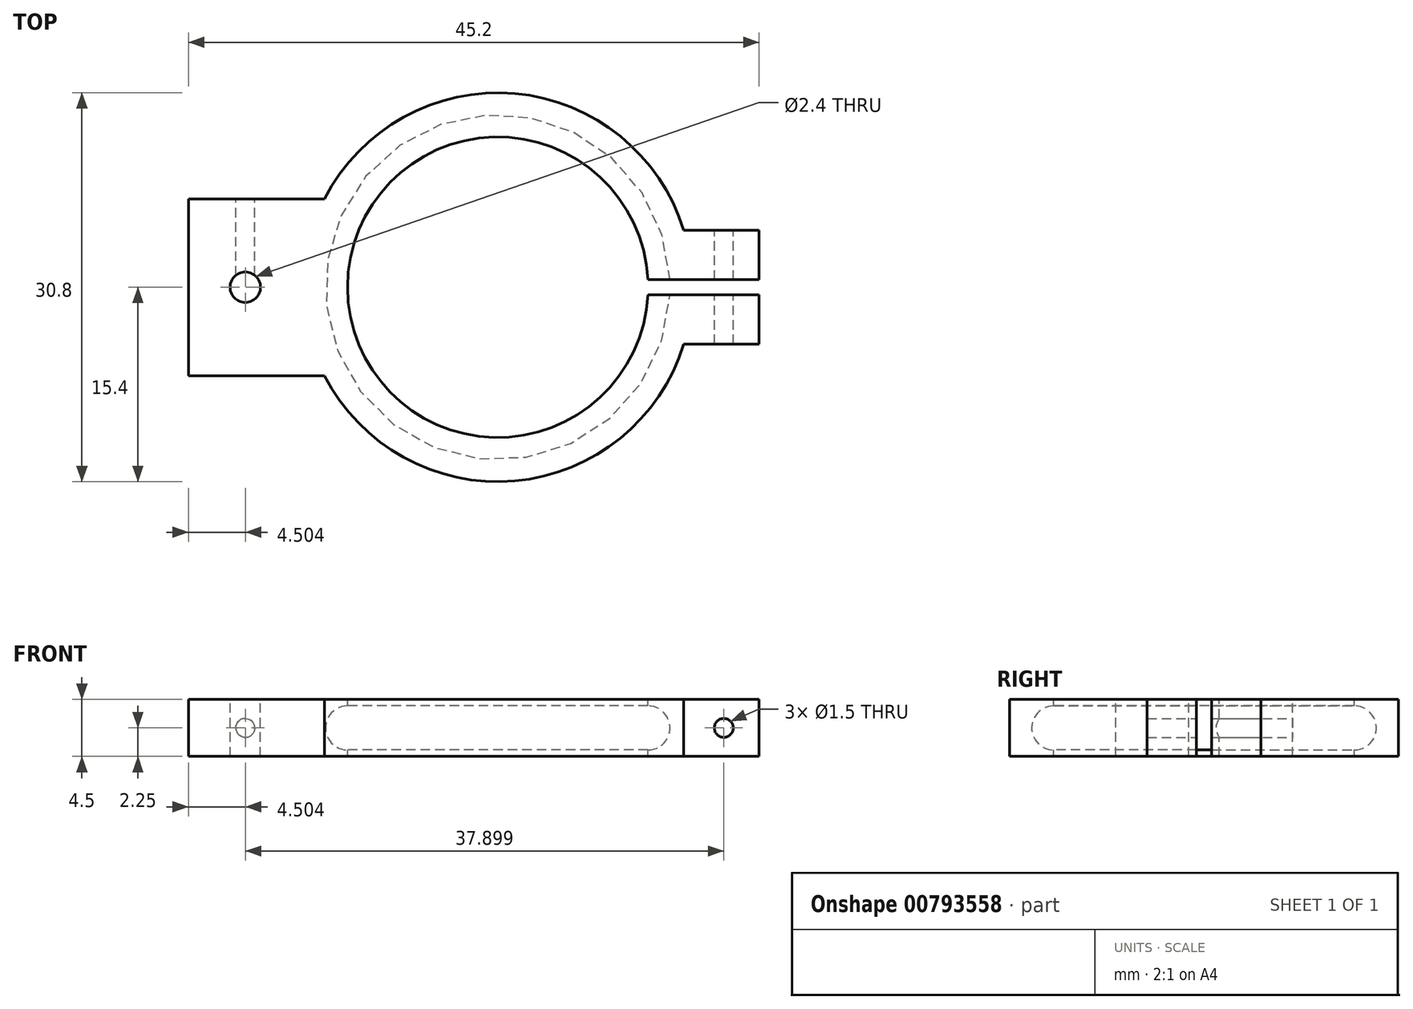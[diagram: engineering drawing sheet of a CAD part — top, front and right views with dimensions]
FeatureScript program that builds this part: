
annotation { "Feature Type Name" : "Feature", "Feature Type Description" : "" }
export const myFeature = defineFeature(function(context is Context, id is Id, definition is map)
    precondition{}
    {
        {
            var Q0;
            Q0=qCreatedBy(makeId("Front.planeOp"),FACE);
            var sketch = newSketch(context, id + "F0", { "sketchPlane" : qUnion([Q0])});
            skCircle(sketch, "E0", {"center": v(-16.3, 0) * mm, "radius": 2.25 * mm});
            skLineSegment(sketch, "E1", {"start": v(-4.4, 3.91) * mm, "end": v(-4.4, -5.05) * mm});
            skLineSegment(sketch, "E2.bottom", {"start": v(-16.3, -2.25) * mm, "end": v(-19.8, -2.25) * mm});
            skLineSegment(sketch, "E2.top", {"start": v(-16.3, 2.25) * mm, "end": v(-19.8, 2.25) * mm});
            skLineSegment(sketch, "E2.left", {"start": v(-16.3, -2.25) * mm, "end": v(-16.3, 2.25) * mm});
            skLineSegment(sketch, "E2.right", {"start": v(-19.8, -2.25) * mm, "end": v(-19.8, 2.25) * mm});
            skArc(sketch, "E3", {"start": v(-16.3, 1.75) * mm, "mid": v(-18.05, 0) * mm, "end": v(-16.3, -1.75) * mm});
            skSolve(sketch);
        }
        {
            var Q0;
            {var subQ1=sQuery(id+"F0.wireOp",EDGE,"E2.bottom");Q0=makeQuery(id+"F0.imprint","IMPRINT",FACE,{"disambiguationData":[TD([[makeQuery(id+"F0.imprint","IMPRINT",EDGE,{"derivedFrom":subQ1}),-1.0]])]});}
            var Q1;
            {var subQ4=sQuery(id+"F0.wireOp",EDGE,"E3");Q1=makeQuery(id+"F0.imprint","IMPRINT",FACE,{"disambiguationData":[TD([[makeQuery(id+"F0.imprint","IMPRINT",EDGE,{"derivedFrom":subQ4}),-1.0]])]});}
            var Q2;
            Q2=sQuery(id+"F0.wireOp",EDGE,"E1");
            revolve(context, id + "F1", {"surfaceOperationType" : NewSurfaceOperationType.NEW, "entities" : qUnion([Q0, Q1]), "axis" : qUnion([Q2]), "revolveType" : RevolveType.FULL});
        }
        {
            var Q0;
            Q0=makeQuery(id+"F1.opRevolve","SWEPT_FACE",FACE,{"disambiguationData":[OSD([sQuery(id+"F0.wireOp",EDGE,"E2.top")])]});
            var sketch = newSketch(context, id + "F2", { "sketchPlane" : qUnion([Q0])});
            skLineSegment(sketch, "E4.bottom", {"start": v(8.93, 4.5) * mm, "end": v(16.3, 4.5) * mm});
            skLineSegment(sketch, "E4.top", {"start": v(8.93, -4.5) * mm, "end": v(16.3, -4.5) * mm});
            skLineSegment(sketch, "E4.left", {"start": v(8.93, 4.5) * mm, "end": v(8.93, -4.5) * mm});
            skLineSegment(sketch, "E4.right", {"start": v(16.3, 4.5) * mm, "end": v(16.3, -4.5) * mm});
            skLineSegment(sketch, "E5.bottom", {"start": v(-16.95, 7) * mm, "end": v(-28.9, 7) * mm});
            skLineSegment(sketch, "E5.top", {"start": v(-16.95, -7) * mm, "end": v(-28.9, -7) * mm});
            skLineSegment(sketch, "E5.left", {"start": v(-16.95, 7) * mm, "end": v(-16.95, -7) * mm});
            skLineSegment(sketch, "E5.right", {"start": v(-28.9, 7) * mm, "end": v(-28.9, -7) * mm});
            skPoint(sketch, "E6", {"position": v(-4.4, 0) * mm});
            skPoint(sketch, "E7", {"position": v(-24.4, 0) * mm});
            skCircle(sketch, "E8", {"center": v(-24.4, 0) * mm, "radius": 1.2 * mm});
            skSolve(sketch);
        }
        {
            var Q0;
            {var subQ0=sQuery(id+"F2.wireOp",EDGE,"E5.right");Q0=makeQuery(id+"F2.imprint","IMPRINT",FACE,{"disambiguationData":[TD([[makeQuery(id+"F2.imprint","IMPRINT",EDGE,{"derivedFrom":subQ0}),1.0]])]});}
            var Q1;
            {var subQ0=sQuery(id+"F2.wireOp",EDGE,"E4.right");Q1=makeQuery(id+"F2.imprint","IMPRINT",FACE,{"disambiguationData":[TD([[makeQuery(id+"F2.imprint","IMPRINT",EDGE,{"derivedFrom":subQ0}),-1.0]])]});}
            extrude(context, id + "F3", {"entities" : qUnion([Q0, Q1]), "operationType" : NewBodyOperationType.ADD, "oppositeDirection" : true, "depth" : 4.5 * mm, "offsetDistance" : 25 * mm});
        }
        {
            var Q0;
            Q0=makeQuery(id+"F3.opExtrude","SWEPT_FACE",FACE,{"disambiguationData":[OSD([sQuery(id+"F2.wireOp",EDGE,"E5.bottom")])]});
            var sketch = newSketch(context, id + "F4", { "sketchPlane" : qUnion([Q0])});
            skCircle(sketch, "E9", {"center": v(24.4, 0) * mm, "radius": 0.75 * mm});
            skSolve(sketch);
        }
        {
            var Q0;
            Q0=makeQuery(id+"F4.imprint","IMPRINT",FACE,{"disambiguationData":[TD([[makeQuery(id+"F4.imprint","IMPRINT",EDGE,{"derivedFrom":sQuery(id+"F4.wireOp",EDGE,"E9")}),1.0]])]});
            extrude(context, id + "F5", {"entities" : qUnion([Q0]), "operationType" : NewBodyOperationType.REMOVE, "oppositeDirection" : true, "depth" : 7 * mm, "offsetDistance" : 25 * mm});
        }
        {
            var Q0;
            Q0=makeQuery(id+"F3.opExtrude","SWEPT_FACE",FACE,{"disambiguationData":[OSD([sQuery(id+"F2.wireOp",EDGE,"E4.bottom")])]});
            var sketch = newSketch(context, id + "F6", { "sketchPlane" : qUnion([Q0])});
            skCircle(sketch, "E10", {"center": v(-13.5, 0) * mm, "radius": 0.75 * mm});
            skSolve(sketch);
        }
        {
            var Q0;
            Q0=makeQuery(id+"F6.imprint","IMPRINT",FACE,{"disambiguationData":[TD([[makeQuery(id+"F6.imprint","IMPRINT",EDGE,{"derivedFrom":sQuery(id+"F6.wireOp",EDGE,"E10")}),1.0]])]});
            extrude(context, id + "F7", {"entities" : qUnion([Q0]), "operationType" : NewBodyOperationType.REMOVE, "oppositeDirection" : true, "depth" : 25 * mm, "offsetDistance" : 25 * mm});
        }
        {
            var Q0;
            {var subQ0=sQuery(id+"F0.wireOp",EDGE,"E2.right");var subQ1=sQuery(id+"F0.wireOp",EDGE,"E2.top");Q0=makeQuery(id+"F3.boolean.opBoolean","MERGE",FACE,{"derivedFrom":[makeQuery(id+"F1.opRevolve","SWEPT_FACE",FACE,{"disambiguationData":[OSD([subQ1])]}),makeQuery(id+"F3.opExtrude","CAP_FACE",FACE,{"disambiguationData":[OSD([subQ1,subQ0,sQuery(id+"F2.wireOp",EDGE,"E4.bottom"),sQuery(id+"F2.wireOp",EDGE,"E4.top"),sQuery(id+"F2.wireOp",EDGE,"E4.right")])],"isStart":true}),makeQuery(id+"F3.opExtrude","CAP_FACE",FACE,{"disambiguationData":[OSD([subQ1,subQ0,sQuery(id+"F2.wireOp",EDGE,"E5.bottom"),sQuery(id+"F2.wireOp",EDGE,"E5.top"),sQuery(id+"F2.wireOp",EDGE,"E5.right"),sQuery(id+"F2.wireOp",EDGE,"E8")])],"isStart":true})]});}
            var sketch = newSketch(context, id + "F8", { "sketchPlane" : qUnion([Q0])});
            skLineSegment(sketch, "E11.bottom", {"start": v(16.3, 0.6) * mm, "end": v(5.02, 0.6) * mm});
            skLineSegment(sketch, "E11.top", {"start": v(16.3, -0.6) * mm, "end": v(5.02, -0.6) * mm});
            skLineSegment(sketch, "E11.left", {"start": v(16.3, 0.6) * mm, "end": v(16.3, -0.6) * mm});
            skLineSegment(sketch, "E11.right", {"start": v(5.02, 0.6) * mm, "end": v(5.02, -0.6) * mm});
            skSolve(sketch);
        }
        {
            var Q0;
            {var subQ0=sQuery(id+"F8.wireOp",EDGE,"E11.right");Q0=makeQuery(id+"F8.imprint","IMPRINT",FACE,{"disambiguationData":[TD([[makeQuery(id+"F8.imprint","IMPRINT",EDGE,{"derivedFrom":subQ0}),1.0]])]});}
            var Q1;
            {var subQ0=sQuery(id+"F8.wireOp",EDGE,"E11.left");Q1=makeQuery(id+"F8.imprint","IMPRINT",FACE,{"disambiguationData":[TD([[makeQuery(id+"F8.imprint","IMPRINT",EDGE,{"derivedFrom":subQ0}),-1.0]])]});}
            extrude(context, id + "F9", {"entities" : qUnion([Q0, Q1]), "operationType" : NewBodyOperationType.REMOVE, "oppositeDirection" : true, "depth" : 25 * mm, "offsetDistance" : 25 * mm});
        }
    });
